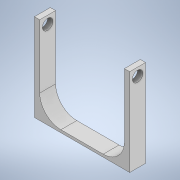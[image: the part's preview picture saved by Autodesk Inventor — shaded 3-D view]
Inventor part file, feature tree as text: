
AUTODESK INVENTOR PART (.ipt)
format: ipt  version: 2021.2 (Build 252289000, 289)  size: 133,632 bytes
history: native  units: in
note: dims shown in document units (in); Inventor stores cm internally (conversion verified against a paired STEP export)
features: extrude x3, sketch x3, fillet x1
ambient origin geometry x8: Origin, YZ Plane, XZ Plane, XY Plane, X Axis, Y Axis, Z Axis, Center Point
bodies: Solid1 (feature_tree)
feature tree (7):
  extrude  "Extrusion1"  Depth=1.5in
  extrude  "Extrusion2"  Depth=0.5in
  extrude  "Extrusion3"  Depth=8.0in TaperAngle=0.0deg
  fillet  "Fillet1"  Radius=1.0in
  sketch  "Sketch1"  dims[d0=9.0in d1=1.5in]
  sketch  "Sketch2"  dims[d2=0.25in d3=0.0in d4=0.5in]
  sketch  "Sketch3"  dims[d5=0.5in d6=8.0in d7=0.0in d8=1.0in d9=0.25in d10=0.0in d11=0.0in d12=2.0in]
